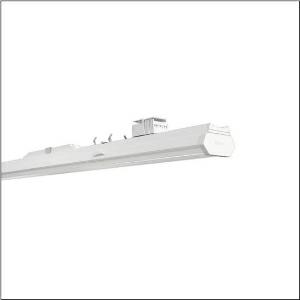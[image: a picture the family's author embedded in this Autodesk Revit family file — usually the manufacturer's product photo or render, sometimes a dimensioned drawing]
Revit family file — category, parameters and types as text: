
# Revit family: licross_r__11_protected_mo_51ts12cn475f_b16d
name_source: partatom
category: Lighting Fixtures
units: mm (PartAtom-declared; Revit-internal decimal feet)

## family parameters
Cut with Voids When Loaded = No
Host = Face
Light Source = No
Part Type = Normal
Room Calculation Point = No
Round Connector Dimension = Use Diameter
Shared = No

## types (1)
- --- (1 x LED, 7680 lm, 49 W, 4000K)
    Apparent Load = 49 VA
    CIE Flux Codes = 54 82 95 97 100
    Color Rendering = 80
    Color Temperature = 4000K
    Default Elevation = 1800 mm
    Description = Licross® 11 Protected MOluminaire insert, length: 1.500mm, width: 90mm, height: 101mm, LED rated luminous flux: 7.680lm, light colour: 840, control gear: ON/OFF Multilumen, CLOi, control gear: ECG Multilumen, with plug, 3-pole, with phase selection, mains connection: 220..240V, AC, 50/60Hz, halogen-free wiring, primary optical cover: cover, of PMMA, light emission: direct with ceiling illumination distribution, protection rating (complete): IP50, insulation class (complete): insulation class I (protective earthing), certification: CE, ENEC, VDE, protection symbol: D if used in an environment with non-conductive dust loads with corresponding accessories, permissible ambient temperature for indoor applications: -35..+40°C, reducing of maximum allowable ambient temperature of 5°C with ceiling mounting, corresponds to IFS (International Featured Standards) requirements for safety and quality in the food industry, packaging unit: 1 piece
    Height = 92 mm
    Lamp = 1 x LED
    Lamp Light Flux = 7680 lm
    Lamp Power = 49 W
    Lamp count = 1
    Length = 1500 mm
    Luminous efficacy = 157 lm/W
    Manufacturer = Siteco
    ModVariant = No
    Model = 51TS12CN475F
    Mounting Place = Ceiling
    Mounting Type = Pendant
    Number of Poles = 1
    OnlyDefault = Yes
    Power Factor = 1
    Product Name = Licross® 11 Protected MO
    Product group = luminaire insert
    ProductGroupID = 902
    Protection Class = Protection class I
    Protection Degree = IP 50
    RLX_Detail_Level = 1
    RlxData = <blob elided: 21857 chars, md5=6e77128a>
    Socket = socket
    Standby Power = 0 W
    System Light Flux = 7680 lm
    System Power = 49 W
    Type Comments = factory setting: luminous flux: 100 % | (A | C | E) | 111 mA
    Type Image = l_1256145.jpg
    URL = http://relux.com
    VarID = @adj_138185
    Voltage = 0 V
    Weight = 0.00 kg
    Width = 88 mm

## geometry (parser evidence)
native form markers: Blend x4, Sweep x11
no freeform markers — native parametric forms only
